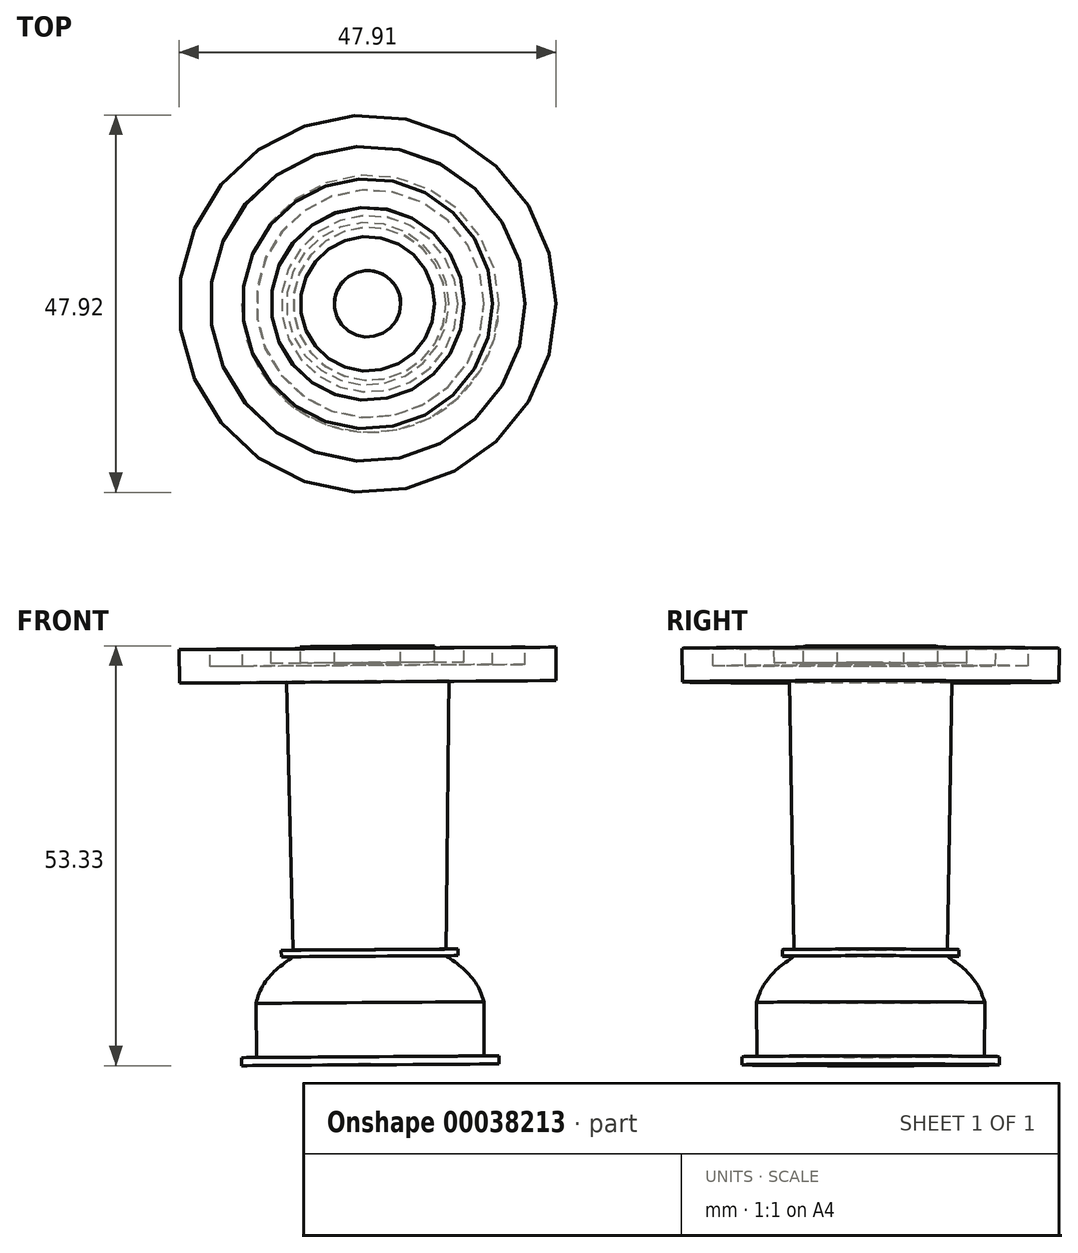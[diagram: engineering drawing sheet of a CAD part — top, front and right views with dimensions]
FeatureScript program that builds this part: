
annotation { "Feature Type Name" : "Feature", "Feature Type Description" : "" }
export const myFeature = defineFeature(function(context is Context, id is Id, definition is map)
    precondition{}
    {
        {
            var Q0;
            Q0=qCreatedBy(makeId("Front.planeOp"),FACE);
            var sketch = newSketch(context, id + "F0", { "sketchPlane" : qUnion([Q0])});
            skLineSegment(sketch, "E0", {"start": v(4.87, 29.8) * mm, "end": v(15.12, 29.8) * mm});
            skLineSegment(sketch, "E1", {"start": v(9.32, -17.87) * mm, "end": v(11.23, -17.87) * mm});
            skLineSegment(sketch, "E2", {"start": v(11.23, -17.87) * mm, "end": v(11.23, -18.89) * mm});
            skLineSegment(sketch, "E3", {"start": v(9.32, -17.87) * mm, "end": v(9.32, -11) * mm});
            skLineSegment(sketch, "E4", {"start": v(4.51, -4.3) * mm, "end": v(6, -4.3) * mm});
            skLineSegment(sketch, "E5", {"start": v(6, -4.3) * mm, "end": v(6, -5.13) * mm});
            skLineSegment(sketch, "E6", {"start": v(6, -5.13) * mm, "end": v(4.5, -5.13) * mm});
            skFitSpline(sketch, "E7", {"points": [v(4.5, -5.13) * mm, v(5.78, -6.06) * mm, v(7, -7.05) * mm, v(8, -8.2) * mm, v(8.7, -9.34) * mm, v(9.32, -11) * mm], "startDerivative": vector(6.4, -4.55) * mm, "endDerivative": vector(2.7, -8.22) * mm});
            skPoint(sketch, "E8.end.orphan", {"position": v(0, -18.89) * mm});
            skLineSegment(sketch, "E9", {"start": v(11.23, -18.89) * mm, "end": v(-5.12, -18.89) * mm});
            skLineSegment(sketch, "E10", {"start": v(4.87, 29.8) * mm, "end": v(4.51, -4.3) * mm});
            skPoint(sketch, "E11.start.orphan", {"position": v(0, 29.8) * mm});
            skLineSegment(sketch, "E12", {"start": v(4.87, 29.8) * mm, "end": v(18.48, 29.8) * mm});
            skPoint(sketch, "E12.endSnap0", {"position": v(10, 29.8) * mm});
            skLineSegment(sketch, "E13", {"start": v(18.48, 29.8) * mm, "end": v(18.48, 34.06) * mm});
            skLineSegment(sketch, "E14", {"start": v(18.48, 34.06) * mm, "end": v(14.55, 34.06) * mm});
            skLineSegment(sketch, "E15", {"start": v(14.55, 34.06) * mm, "end": v(14.55, 31.84) * mm});
            skLineSegment(sketch, "E16", {"start": v(14.55, 31.84) * mm, "end": v(10.41, 31.84) * mm});
            skLineSegment(sketch, "E17", {"start": v(10.41, 31.84) * mm, "end": v(10.41, 33.96) * mm});
            skLineSegment(sketch, "E18", {"start": v(10.41, 33.96) * mm, "end": v(6.78, 33.96) * mm});
            skLineSegment(sketch, "E19", {"start": v(6.78, 33.96) * mm, "end": v(6.78, 32.14) * mm});
            skLineSegment(sketch, "E20", {"start": v(6.78, 32.14) * mm, "end": v(3.06, 32.14) * mm});
            skLineSegment(sketch, "E21", {"start": v(3.06, 32.14) * mm, "end": v(3.06, 34.22) * mm});
            skLineSegment(sketch, "E22", {"start": v(3.06, 34.22) * mm, "end": v(-1.26, 34.22) * mm});
            skLineSegment(sketch, "E23", {"start": v(-1.26, 34.22) * mm, "end": v(-1.26, 31.94) * mm});
            skLineSegment(sketch, "E24", {"start": v(-1.26, 31.94) * mm, "end": v(-5.46, 31.94) * mm});
            skLineSegment(sketch, "E25", {"start": v(-5.46, 31.94) * mm, "end": v(-5.12, -18.89) * mm});
            skSolve(sketch);
        }
        {
            var Q0;
            Q0=makeQuery(id+"F0.imprint","IMPRINT",FACE,{"disambiguationData":[TD([[makeQuery(id+"F0.imprint","IMPRINT",EDGE,{"derivedFrom":sQuery(id+"F0.wireOp",EDGE,"E1")}),-1.0]])]});
            var Q1;
            Q1=sQuery(id+"F0.wireOp",EDGE,"E25");
            revolve(context, id + "F1", {"entities" : qUnion([Q0]), "axis" : qUnion([Q1]), "revolveType" : RevolveType.FULL});
        }
    });
